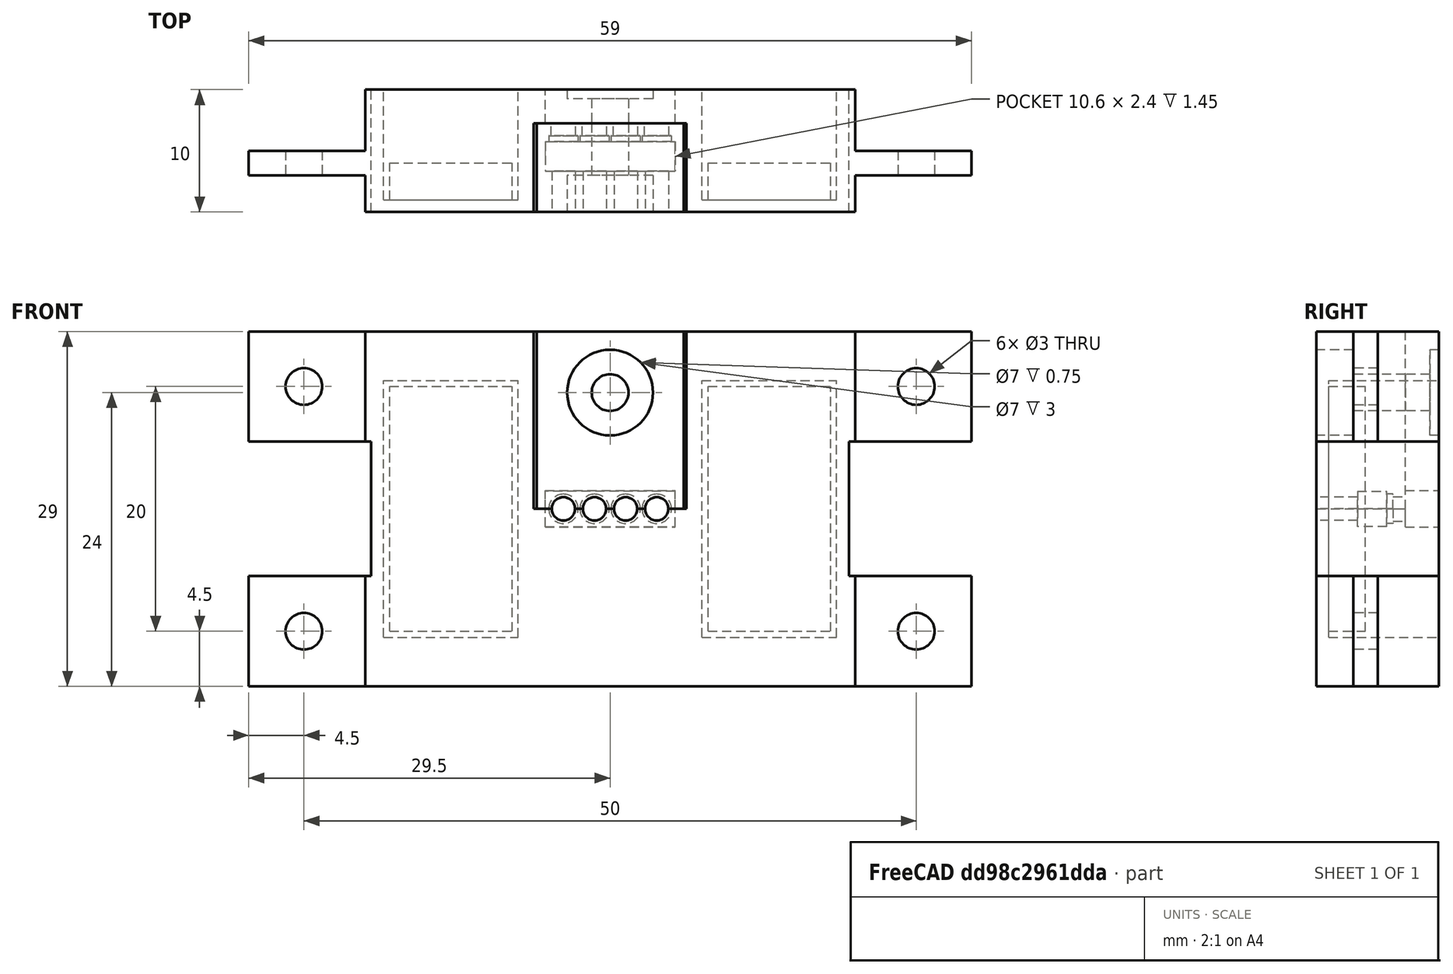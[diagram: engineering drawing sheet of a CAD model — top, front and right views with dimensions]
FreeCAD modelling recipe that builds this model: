
FCSTD DOCUMENT  (FreeCAD 0.16R6712 (Git))
Label: Conector
License: All rights reserved
LicenseURL: http://en.wikipedia.org/wiki/All_rights_reserved
objects: Part::Box×14, Part::Cut×13, Part::Cylinder×11, Part::FeaturePython×10, Part::MultiFuse×9, Part::Offset×2
note: 59 computed .brp shape members not serialized (recipe doc carries the construction recipe); baked Part::Feature solids carry a one-line shape summary decoded from their .brp

FEATURE [Part::Cylinder] Cylinder003  label="Cilindro003"
  Angle = 360
  Height = 5.35
  Radius = 0.75
FEATURE [Part::FeaturePython] Array004  # Draft array (typed FeaturePython)
  Angle = 360
  ArrayType = 0
  Axis = (0,0,1)
  Base = -> Cylinder003
  Center = (0,0,0)
  Fuse = false
  IntervalAxis = (0,0,0)
  IntervalX = (0,0,0)
  IntervalY = (0,2.54,0)
  IntervalZ = (0,0,0)
  NumberPolar = 1
  NumberX = 1
  NumberY = 4
  NumberZ = 1
  Placement = pos=(1.25,1.29,0) rot=(0,0,1;0rad)
FEATURE [Part::Box] Box005  label="Cubo005"
  Height = 2
  Length = 2.5
  Width = 10.2
FEATURE [Part::Cylinder] Cylinder004  label="Cilindro004"
  Angle = 360
  Height = 0.5
  Radius = 1
FEATURE [Part::Cylinder] Cylinder005  label="Cilindro005"
  Angle = 360
  Height = 1
  Placement = pos=(0,0,0) rot=(0,1,0;3.14159rad)
  Radius = 0.8
FEATURE [Part::MultiFuse] Fusion004
  Shapes = -> [Cylinder004,Cylinder005]
FEATURE [Part::FeaturePython] Array005  # Draft array (typed FeaturePython)
  Angle = 360
  ArrayType = 0
  Axis = (0,0,1)
  Base = -> Fusion004
  Center = (0,0,0)
  Fuse = false
  IntervalAxis = (0,0,0)
  IntervalX = (0,0,0)
  IntervalY = (0,2.54,0)
  IntervalZ = (0,0,0)
  NumberPolar = 1
  NumberX = 1
  NumberY = 4
  NumberZ = 1
  Placement = pos=(1.25,1.29,-0.5) rot=(0,0,1;0rad)
FEATURE [Part::MultiFuse] Fusion005
  Shapes = -> [Array004,Array005]
FEATURE [Part::MultiFuse] Fusion006  label="PogoPin001"
  Placement = pos=(10.2,0,0) rot=(0.57735,-0.57735,0.57735;2.0944rad)
  Shapes = -> [Box005,Fusion005]
FEATURE [Part::Offset] Offset001  label="PogoPin_Funda_2"
  Fill = false
  Intersection = false
  Join = 2
  Mode = 0
  Placement = pos=(0.9,5.55,13.25) rot=(0,0,1;0rad)
  SelfIntersection = false
  Source = -> Fusion006
  Value = 0.2
FEATURE [Part::Box] Box013  label="Cubo013"
  Height = 20
  Length = 10
  Width = 3
FEATURE [Part::FeaturePython] Array007  label="Imanes20x10x3"  # Draft array (typed FeaturePython)
  Angle = 360
  ArrayType = 0
  Axis = (0,0,1)
  Base = -> Box013
  Center = (0,0,0)
  Fuse = false
  IntervalAxis = (0,0,0)
  IntervalX = (26,0,0)
  IntervalY = (0,0,0)
  IntervalZ = (0,0,0)
  NumberPolar = 1
  NumberX = 2
  NumberY = 1
  NumberZ = 1
  Placement = pos=(11.5,1,4.5) rot=(0,0,1;0rad)
FEATURE [Part::Box] Box014  label="Base_Conector"
  Height = 29
  Length = 59
  Width = 10
FEATURE [Part::Box] Box015  label="RecorteBase_1"
  Height = 9
  Length = 9.5
  Width = 2
FEATURE [Part::Box] Box016  label="RecorteBase_2"
  Height = 29
  Length = 9.5
  Width = 10
FEATURE [Part::FeaturePython] Array008  label="RecortesBase_1"  # Draft array (typed FeaturePython)
  Angle = 360
  ArrayType = 0
  Axis = (0,0,1)
  Base = -> Box015
  Center = (0,0,0)
  Fuse = false
  IntervalAxis = (0,0,0)
  IntervalX = (49.5,0,0)
  IntervalY = (0,0,20)
  IntervalZ = (0,0,0)
  NumberPolar = 1
  NumberX = 2
  NumberY = 2
  NumberZ = 1
  Placement = pos=(0,3,0) rot=(0,0,1;0rad)
FEATURE [Part::FeaturePython] Array009  label="RecortesBase_2"  # Draft array (typed FeaturePython)
  Angle = 360
  ArrayType = 0
  Axis = (0,0,1)
  Base = -> Box016
  Center = (0,0,0)
  Fuse = false
  IntervalAxis = (0,0,0)
  IntervalX = (49.5,0,0)
  IntervalY = (0,0,0)
  IntervalZ = (0,0,0)
  NumberPolar = 1
  NumberX = 2
  NumberY = 1
  NumberZ = 1
FEATURE [Part::Box] Box017  label="RecorteBase_3"
  Height = 11
  Length = 0.5
  Width = 10
FEATURE [Part::FeaturePython] Array010  label="RecortesBase_3"  # Draft array (typed FeaturePython)
  Angle = 360
  ArrayType = 0
  Axis = (0,0,1)
  Base = -> Box017
  Center = (0,0,0)
  Fuse = false
  IntervalAxis = (0,0,0)
  IntervalX = (39.5,0,0)
  IntervalY = (0,0,0)
  IntervalZ = (0,0,0)
  NumberPolar = 1
  NumberX = 2
  NumberY = 1
  NumberZ = 1
  Placement = pos=(9.5,0,9) rot=(0,0,1;0rad)
FEATURE [Part::Cut] Cut
  Base = -> Array009
  Tool = -> Array008
FEATURE [Part::MultiFuse] Fusion007  label="Base_Conector_Recorte"
  Shapes = -> [Array010,Cut]
FEATURE [Part::Cut] Cut001  label="Base_Conector_1"
  Base = -> Box014
  Tool = -> Fusion007
FEATURE [Part::Cylinder] Cylinder006  label="Agujero_Soporte"
  Angle = 360
  Height = 10
  Placement = pos=(0,0,0) rot=(1,0,0;1.5708rad)
  Radius = 1.5
FEATURE [Part::FeaturePython] Array011  label="Agujeros_Soporte"  # Draft array (typed FeaturePython)
  Angle = 360
  ArrayType = 0
  Axis = (0,0,1)
  Base = -> Cylinder006
  Center = (0,0,0)
  Fuse = false
  IntervalAxis = (0,0,0)
  IntervalX = (50,0,0)
  IntervalY = (0,0,20)
  IntervalZ = (0,0,0)
  NumberPolar = 1
  NumberX = 2
  NumberY = 2
  NumberZ = 1
  Placement = pos=(4.5,9,4.5) rot=(0,0,1;0rad)
FEATURE [Part::Cut] Cut002  label="Base_Conector_2"
  Base = -> Cut001
  Tool = -> Array011
FEATURE [Part::Box] Box018  label="Hueco_Conectores"
  Height = 29
  Length = 12
  Placement = pos=(23.5,0,0) rot=(0,0,1;0rad)
  Width = 10
FEATURE [Part::Cut] Cut003  label="Base_Conector_3"
  Base = -> Cut002
  Tool = -> Box018
FEATURE [Part::Box] Box019  label="HuecoIman"
  Height = 21
  Length = 11
  Placement = pos=(11,1,4) rot=(0,0,1;0rad)
  Width = 9
FEATURE [Part::FeaturePython] Array012  label="HuecosImanes"  # Draft array (typed FeaturePython)
  Angle = 360
  ArrayType = 0
  Axis = (0,0,1)
  Base = -> Box019
  Center = (0,0,0)
  Fuse = false
  IntervalAxis = (0,0,0)
  IntervalX = (26,0,0)
  IntervalY = (0,0,0)
  IntervalZ = (0,0,0)
  NumberPolar = 1
  NumberX = 2
  NumberY = 1
  NumberZ = 1
FEATURE [Part::Cut] Cut004  label="Base_Conector_4"
  Base = -> Cut003
  Tool = -> Array012
FEATURE [Part::Box] Box020  label="ConectoresINF_base"
  Height = 14.5
  Length = 12
  Width = 10
FEATURE [Part::Cylinder] Cylinder007  label="Cilindro006"
  Angle = 360
  Height = 5.35
  Radius = 0.75
FEATURE [Part::FeaturePython] Array013  # Draft array (typed FeaturePython)
  Angle = 360
  ArrayType = 0
  Axis = (0,0,1)
  Base = -> Cylinder007
  Center = (0,0,0)
  Fuse = false
  IntervalAxis = (0,0,0)
  IntervalX = (0,0,0)
  IntervalY = (0,2.54,0)
  IntervalZ = (0,0,0)
  NumberPolar = 1
  NumberX = 1
  NumberY = 4
  NumberZ = 1
  Placement = pos=(1.25,1.29,0) rot=(0,0,1;0rad)
FEATURE [Part::Box] Box021  label="Cubo014"
  Height = 2
  Length = 2.5
  Width = 10.2
FEATURE [Part::Cylinder] Cylinder008  label="Cilindro007"
  Angle = 360
  Height = 0.5
  Radius = 1
FEATURE [Part::Cylinder] Cylinder009  label="Cilindro008"
  Angle = 360
  Height = 1
  Placement = pos=(0,0,0) rot=(0,1,0;3.14159rad)
  Radius = 0.8
FEATURE [Part::MultiFuse] Fusion008
  Shapes = -> [Cylinder008,Cylinder009]
FEATURE [Part::FeaturePython] Array014  # Draft array (typed FeaturePython)
  Angle = 360
  ArrayType = 0
  Axis = (0,0,1)
  Base = -> Fusion008
  Center = (0,0,0)
  Fuse = false
  IntervalAxis = (0,0,0)
  IntervalX = (0,0,0)
  IntervalY = (0,2.54,0)
  IntervalZ = (0,0,0)
  NumberPolar = 1
  NumberX = 1
  NumberY = 4
  NumberZ = 1
  Placement = pos=(1.25,1.29,-0.5) rot=(0,0,1;0rad)
FEATURE [Part::MultiFuse] Fusion009
  Shapes = -> [Array013,Array014]
FEATURE [Part::MultiFuse] Fusion010  label="PogoPin002"
  Placement = pos=(10.2,0,0) rot=(0.57735,-0.57735,0.57735;2.0944rad)
  Shapes = -> [Box021,Fusion009]
FEATURE [Part::Offset] Offset002  label="PogoPin_Funda"
  Fill = false
  Intersection = false
  Join = 2
  Mode = 0
  Placement = pos=(0.9,5.55,13.25) rot=(0,0,1;0rad)
  SelfIntersection = false
  Source = -> Fusion010
  Value = 0.2
FEATURE [Part::Cut] Cut005  label="ConectoresINF_base_2"
  Base = -> Box020
  Tool = -> Offset001
FEATURE [Part::Box] Box  label="HuecoCablesINF"
  Height = 3
  Length = 10.6
  Placement = pos=(0.7,7.25,13) rot=(0,0,1;0rad)
  Width = 2.75
FEATURE [Part::Box] Box022  label="ParedConectores"
  Height = 14.5
  Length = 12
  Placement = pos=(0,7.25,14.5) rot=(0,0,1;0rad)
  Width = 2.75
FEATURE [Part::MultiFuse] Fusion  label="ConectoresINF_base_3"
  Shapes = -> [Cut005,Box022]
FEATURE [Part::Cut] Cut006  label="ConectoresINF_base_4"
  Base = -> Fusion
  Tool = -> Box
FEATURE [Part::Box] Box023  label="ConectoresSUP_base_1"
  Height = 14.5
  Length = 12
  Placement = pos=(0,0,14.5) rot=(0,0,1;0rad)
  Width = 7.25
FEATURE [Part::Cylinder] Cylinder  label="AgujeroTornilloINF"
  Angle = 360
  Height = 3
  Placement = pos=(6,10.25,24) rot=(1,0,0;1.5708rad)
  Radius = 1.5
FEATURE [Part::Cut] Cut007  label="ConectoresINF"
  Base = -> Cut006
  Placement = pos=(23.5,0,0) rot=(0,0,1;0rad)
  Tool = -> Cylinder
FEATURE [Part::Cut] Cut008  label="ConectoresSUP_base_2"
  Base = -> Box023
  Tool = -> Offset002
FEATURE [Part::Cylinder] Cylinder010  label="AgujeroTornilloExtSup"
  Angle = 360
  Height = 3
  Placement = pos=(6,3,24) rot=(1,0,0;1.5708rad)
  Radius = 3.5
FEATURE [Part::Cut] Cut009  label="ConectoresSUP_base_3"
  Base = -> Cut008
  Tool = -> Cylinder010
FEATURE [Part::Cylinder] Cylinder011  label="AgujeroTornilloIntSup"
  Angle = 360
  Height = 4.25
  Placement = pos=(6,7.25,24) rot=(1,0,0;1.5708rad)
  Radius = 1.5
FEATURE [Part::Cut] Cut010  label="Conector_ParteSUP"
  Base = -> Cut009
  Placement = pos=(23.5,0,0) rot=(0,0,1;0rad)
  Tool = -> Cylinder011
FEATURE [Part::Box] Box024  label="HuecoSUP"
  Height = 14.5
  Length = 12.5
  Placement = pos=(23.25,0,14.5) rot=(0,0,1;0rad)
  Width = 7.25
FEATURE [Part::Cut] Cut011  label="Base_Conector_5"
  Base = -> Cut004
  Tool = -> Box024
FEATURE [Part::MultiFuse] Fusion011  label="Base_Conector_6"
  Shapes = -> [Cut007,Cut011]
FEATURE [Part::Cylinder] Cylinder012  label="HuecoTornilloEXT"
  Angle = 360
  Height = 0.75
  Placement = pos=(29.5,10,24) rot=(1,0,0;1.5708rad)
  Radius = 3.5
FEATURE [Part::Cut] Cut012  label="Conector_ParteINF"
  Base = -> Fusion011
  Tool = -> Cylinder012
